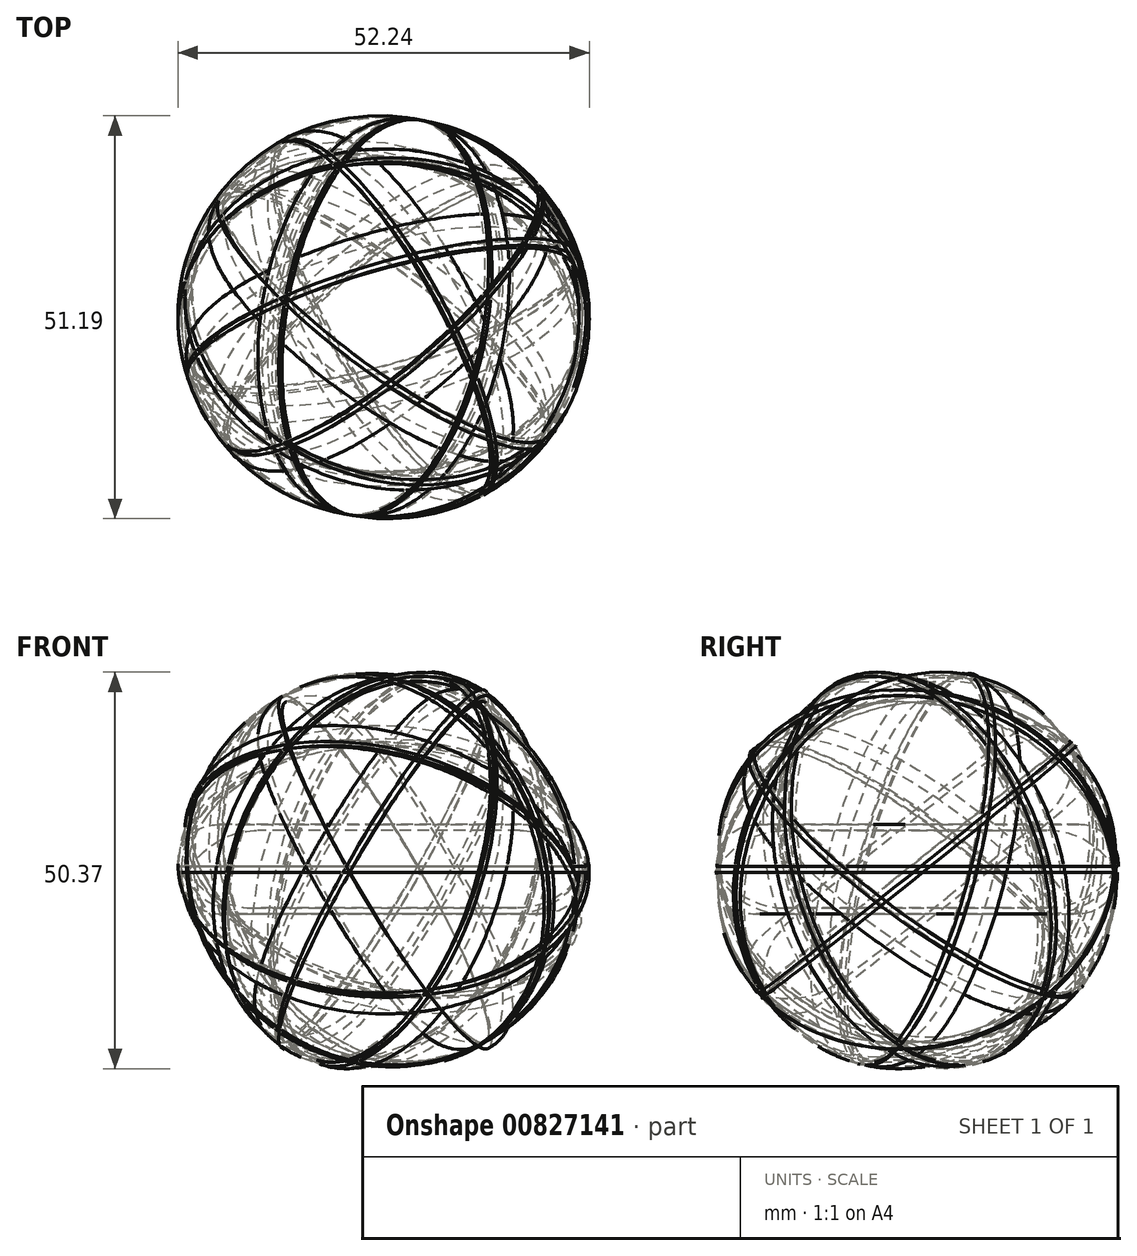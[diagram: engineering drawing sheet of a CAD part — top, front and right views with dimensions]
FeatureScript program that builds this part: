
annotation { "Feature Type Name" : "Feature", "Feature Type Description" : "" }
export const myFeature = defineFeature(function(context is Context, id is Id, definition is map)
    precondition{}
    {
        {
            var Q0;
            Q0=qCreatedBy(makeId("Top.planeOp"),FACE);
            var sketch = newSketch(context, id + "F0", { "sketchPlane" : qUnion([Q0])});
            skCircle(sketch, "E0", {"center": v(0, 0) * mm, "radius": 25.48 * mm});
            skSolve(sketch);
        }
        {
            var Q0;
            Q0=makeQuery(id+"F0.imprint","IMPRINT",FACE,{"disambiguationData":[TD([[makeQuery(id+"F0.imprint","IMPRINT",EDGE,{"derivedFrom":sQuery(id+"F0.wireOp",EDGE,"E0")}),1.0]])]});
            extrude(context, id + "F1", {"entities" : qUnion([Q0]), "depth" : 5.3 * mm, "offsetDistance" : 25 * mm});
        }
        {
            var Q0;
            Q0=makeQuery(id+"F1.opExtrude","CAP_FACE",FACE,{"disambiguationData":[OSD([sQuery(id+"F0.wireOp",EDGE,"E0")])],"isStart":true});
            var sketch = newSketch(context, id + "F2", { "sketchPlane" : qUnion([Q0])});
            skLineSegment(sketch, "E1", {"start": v(15.73, -89.6) * mm, "end": v(-12.25, 65.47) * mm});
            skSolve(sketch);
        }
        {
            var Q0;
            Q0=makeQuery(id+"F1.opExtrude","SWEPT_BODY",BODY,{"disambiguationData":[OSD([sQuery(id+"F0.wireOp",EDGE,"E0")])]});
            var Q1;
            Q1=sQuery(id+"F2.wireOp",EDGE,"E1");
            circularPattern(context, id + "F3", {"entities" : qUnion([Q0]), "axis" : qUnion([Q1]), "angle" : 360 * degree, "instanceCount" : 6, "equalSpace" : true, "isCentered" : true});
        }
        {
            var Q0;
            Q0=makeQuery(id+"F3.opPattern","COPY",EDGE,{"derivedFrom":makeQuery(id+"F1.opExtrude","CAP_EDGE",EDGE,{"disambiguationData":[OSD([sQuery(id+"F0.wireOp",EDGE,"E0")])],"isStart":false}),"instanceName":"-4"});
            var Q1;
            Q1=makeQuery(id+"F3.opPattern","COPY",EDGE,{"derivedFrom":makeQuery(id+"F1.opExtrude","CAP_EDGE",EDGE,{"disambiguationData":[OSD([sQuery(id+"F0.wireOp",EDGE,"E0")])],"isStart":false}),"instanceName":"-1"});
            var Q2;
            Q2=makeQuery(id+"F3.opPattern","COPY",EDGE,{"derivedFrom":makeQuery(id+"F1.opExtrude","CAP_EDGE",EDGE,{"disambiguationData":[OSD([sQuery(id+"F0.wireOp",EDGE,"E0")])],"isStart":false}),"instanceName":"-3"});
            var Q3;
            Q3=makeQuery(id+"F1.opExtrude","CAP_EDGE",EDGE,{"disambiguationData":[OSD([sQuery(id+"F0.wireOp",EDGE,"E0")])],"isStart":false});
            var Q4;
            Q4=makeQuery(id+"F3.opPattern","COPY",EDGE,{"derivedFrom":makeQuery(id+"F1.opExtrude","CAP_EDGE",EDGE,{"disambiguationData":[OSD([sQuery(id+"F0.wireOp",EDGE,"E0")])],"isStart":false}),"instanceName":"-2"});
            var Q5;
            Q5=makeQuery(id+"F3.opPattern","COPY",EDGE,{"derivedFrom":makeQuery(id+"F1.opExtrude","CAP_EDGE",EDGE,{"disambiguationData":[OSD([sQuery(id+"F0.wireOp",EDGE,"E0")])],"isStart":false}),"instanceName":"-5"});
            fillet(context, id + "F4", {"entities" : qUnion([Q0, Q1, Q2, Q3, Q4, Q5]), "radius" : 10 * mm, "tangentPropagation" : true, "allowEdgeOverflow" : false});
        }
        {
            var Q0;
            Q0=makeQuery(id+"F3.opPattern","COPY",EDGE,{"derivedFrom":makeQuery(id+"F1.opExtrude","CAP_EDGE",EDGE,{"disambiguationData":[OSD([sQuery(id+"F0.wireOp",EDGE,"E0")])],"isStart":false}),"instanceName":"3"});
            var Q1;
            Q1=makeQuery(id+"F3.opPattern","COPY",EDGE,{"derivedFrom":makeQuery(id+"F1.opExtrude","CAP_EDGE",EDGE,{"disambiguationData":[OSD([sQuery(id+"F0.wireOp",EDGE,"E0")])],"isStart":false}),"instanceName":"5"});
            var Q2;
            Q2=makeQuery(id+"F3.opPattern","COPY",EDGE,{"derivedFrom":makeQuery(id+"F1.opExtrude","CAP_EDGE",EDGE,{"disambiguationData":[OSD([sQuery(id+"F0.wireOp",EDGE,"E0")])],"isStart":false}),"instanceName":"2"});
            var Q3;
            Q3=makeQuery(id+"F3.opPattern","COPY",EDGE,{"derivedFrom":makeQuery(id+"F1.opExtrude","CAP_EDGE",EDGE,{"disambiguationData":[OSD([sQuery(id+"F0.wireOp",EDGE,"E0")])],"isStart":false}),"instanceName":"4"});
            var Q4;
            Q4=makeQuery(id+"F3.opPattern","COPY",EDGE,{"derivedFrom":makeQuery(id+"F1.opExtrude","CAP_EDGE",EDGE,{"disambiguationData":[OSD([sQuery(id+"F0.wireOp",EDGE,"E0")])],"isStart":false}),"instanceName":"1"});
            fillet(context, id + "F5", {"entities" : qUnion([Q0, Q1, Q2, Q3, Q4]), "radius" : 5 * mm, "tangentPropagation" : true, "allowEdgeOverflow" : false});
        }
        {
            var Q0;
            Q0=makeQuery(id+"F3.opPattern","COPY",BODY,{"derivedFrom":makeQuery(id+"F1.opExtrude","SWEPT_BODY",BODY,{"disambiguationData":[OSD([sQuery(id+"F0.wireOp",EDGE,"E0")])]}),"instanceName":"3"});
            var Q1;
            Q1=makeQuery(id+"F1.opExtrude","SWEPT_BODY",BODY,{"disambiguationData":[OSD([sQuery(id+"F0.wireOp",EDGE,"E0")])]});
            var Q2;
            Q2=makeQuery(id+"F3.opPattern","COPY",BODY,{"derivedFrom":makeQuery(id+"F1.opExtrude","SWEPT_BODY",BODY,{"disambiguationData":[OSD([sQuery(id+"F0.wireOp",EDGE,"E0")])]}),"instanceName":"2"});
            var Q3;
            Q3=makeQuery(id+"F3.opPattern","COPY",BODY,{"derivedFrom":makeQuery(id+"F1.opExtrude","SWEPT_BODY",BODY,{"disambiguationData":[OSD([sQuery(id+"F0.wireOp",EDGE,"E0")])]}),"instanceName":"4"});
            var Q4;
            Q4=makeQuery(id+"F3.opPattern","COPY",BODY,{"derivedFrom":makeQuery(id+"F1.opExtrude","SWEPT_BODY",BODY,{"disambiguationData":[OSD([sQuery(id+"F0.wireOp",EDGE,"E0")])]}),"instanceName":"-5"});
            var Q5;
            {var subQ0=sQuery(id+"F0.wireOp",EDGE,"E0");Q5=makeQuery(id+"F4.opFillet","BLEND_EDGE",EDGE,{"blendedFrom":[makeQuery(id+"F3.opPattern","COPY",EDGE,{"derivedFrom":makeQuery(id+"F1.opExtrude","CAP_EDGE",EDGE,{"disambiguationData":[OSD([subQ0])],"isStart":false}),"instanceName":"-4"}),makeQuery(id+"F3.opPattern","COPY",FACE,{"derivedFrom":makeQuery(id+"F1.opExtrude","CAP_FACE",FACE,{"disambiguationData":[OSD([subQ0])],"isStart":true}),"instanceName":"-4"})],"blendedInto":[makeQuery(id+"F3.opPattern","COPY",FACE,{"derivedFrom":makeQuery(id+"F1.opExtrude","CAP_FACE",FACE,{"disambiguationData":[OSD([subQ0])],"isStart":true}),"instanceName":"-4"})]});}
            circularPattern(context, id + "F6", {"entities" : qUnion([Q0, Q1, Q2, Q3, Q4]), "axis" : qUnion([Q5]), "angle" : 360 * degree, "instanceCount" : 8, "equalSpace" : true});
        }
    });
